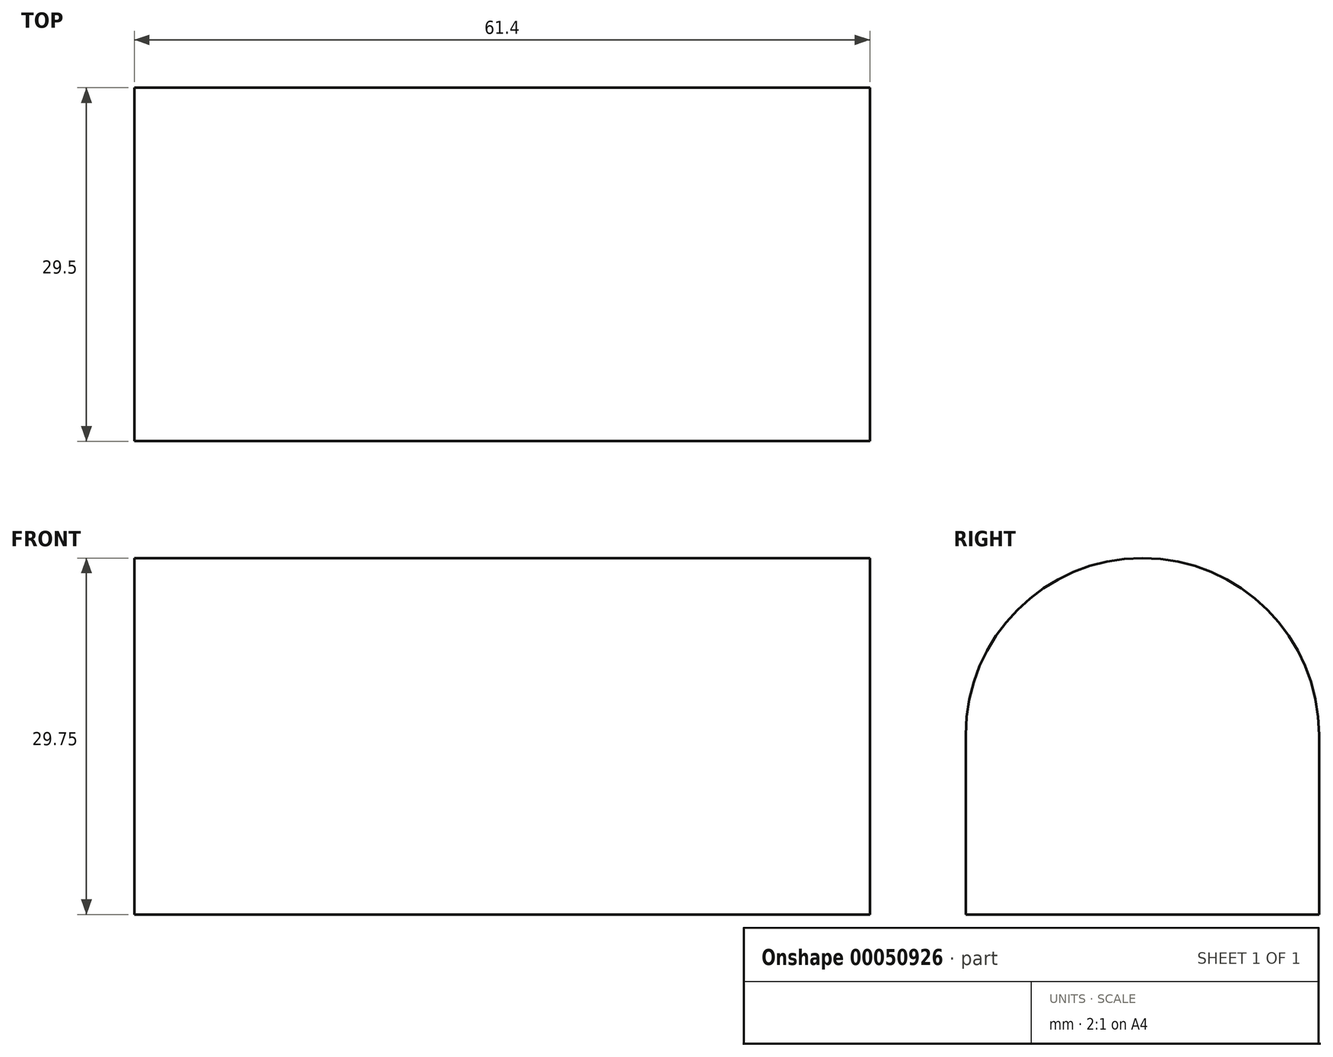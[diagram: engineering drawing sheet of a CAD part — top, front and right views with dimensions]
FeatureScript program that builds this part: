
annotation { "Feature Type Name" : "Feature", "Feature Type Description" : "" }
export const myFeature = defineFeature(function(context is Context, id is Id, definition is map)
    precondition{}
    {
        {
            var Q0;
            Q0=qCreatedBy(makeId("Top.planeOp"),FACE);
            var sketch = newSketch(context, id + "F0", { "sketchPlane" : qUnion([Q0])});
            skLineSegment(sketch, "E0.bottom", {"start": v(-28.71, 16.88) * mm, "end": v(32.69, 16.88) * mm});
            skLineSegment(sketch, "E0.top", {"start": v(-28.71, -12.62) * mm, "end": v(32.69, -12.62) * mm});
            skLineSegment(sketch, "E0.left", {"start": v(-28.71, 16.88) * mm, "end": v(-28.71, -12.62) * mm});
            skLineSegment(sketch, "E0.right", {"start": v(32.69, 16.88) * mm, "end": v(32.69, -12.62) * mm});
            skSolve(sketch);
        }
        {
            var Q0;
            Q0=makeQuery(id+"F0.imprint","IMPRINT",FACE,{"disambiguationData":[TD([[makeQuery(id+"F0.imprint","IMPRINT",EDGE,{"derivedFrom":sQuery(id+"F0.wireOp",EDGE,"E0.bottom")}),-1.0]])]});
            var Q1;
            Q1 = qSketchRegion(id + "F2", true);
            extrude(context, id + "F1", {"entities" : qUnion([Q0, Q1]), "depth" : 30 * mm});
        }
        {
            var Q0;
            Q0=makeQuery(id+"F1.opExtrude","SWEPT_FACE",FACE,{"disambiguationData":[OSD([sQuery(id+"F0.wireOp",EDGE,"E0.right")])]});
            var sketch = newSketch(context, id + "F2", { "sketchPlane" : qUnion([Q0])});
            skLineSegment(sketch, "E1", {"start": v(-4.87, 30) * mm, "end": v(9.13, 30) * mm});
            skLineSegment(sketch, "E2", {"start": v(16.88, 0) * mm, "end": v(16.88, 15) * mm});
            skLineSegment(sketch, "E3", {"start": v(-12.62, 0) * mm, "end": v(-12.62, 15) * mm});
            skArc(sketch, "E4", {"start": v(-12.62, 15) * mm, "mid": v(2.13, 29.75) * mm, "end": v(16.88, 15) * mm});
            skSolve(sketch);
        }
        {
            var Q0;
            {var subQ7=sQuery(id+"F2.wireOp",EDGE,"E1");Q0=makeQuery(id+"F2.imprint","IMPRINT",FACE,{"disambiguationData":[TD([[makeQuery(id+"F2.imprint","IMPRINT",EDGE,{"derivedFrom":subQ7}),1.0]])]});}
            extrude(context, id + "F3", {"entities" : qUnion([Q0]), "operationType" : NewBodyOperationType.REMOVE, "endBound" : BoundingType.UP_TO_NEXT, "oppositeDirection" : true, "depth" : 25 * mm});
        }
    });
